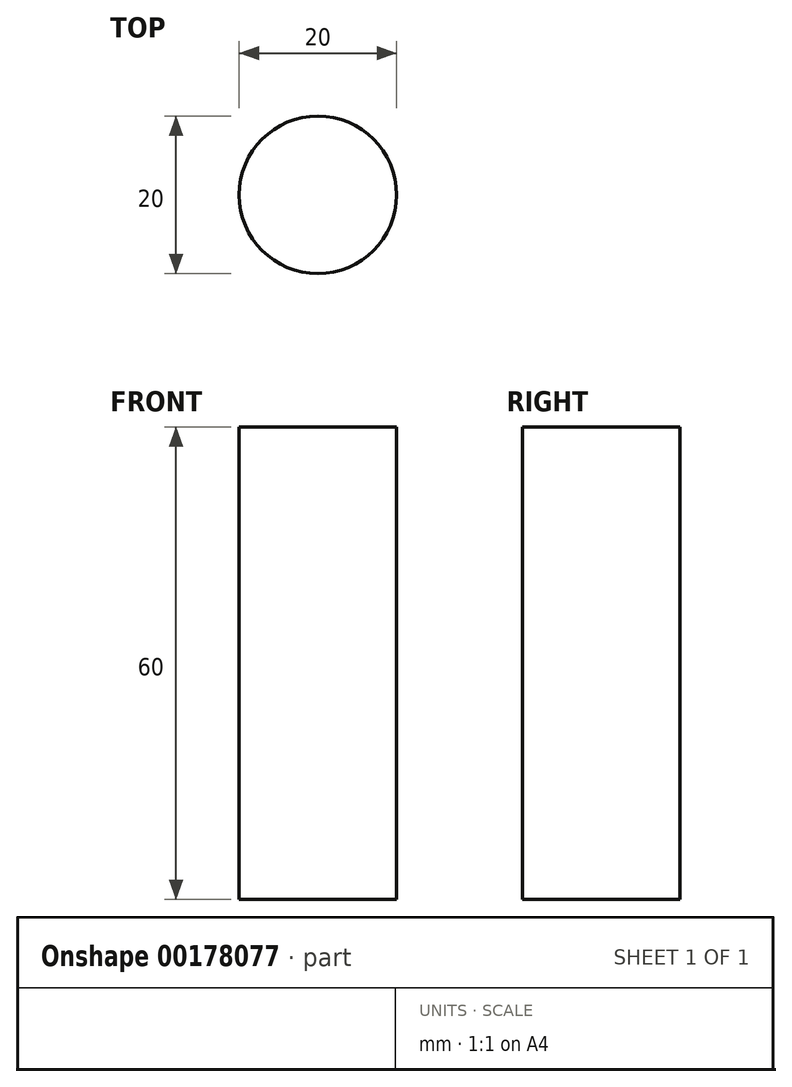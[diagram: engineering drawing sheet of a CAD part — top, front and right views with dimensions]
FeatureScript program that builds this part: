
annotation { "Feature Type Name" : "Feature", "Feature Type Description" : "" }
export const myFeature = defineFeature(function(context is Context, id is Id, definition is map)
    precondition{}
    {
        {
            var Q0;
            Q0=qCreatedBy(makeId("Top.planeOp"),FACE);
            var sketch = newSketch(context, id + "F0", { "sketchPlane" : qUnion([Q0])});
            skCircle(sketch, "E0", {"center": v(0, 0) * mm, "radius": 10 * mm});
            skSolve(sketch);
        }
        {
            var Q0;
            Q0 = qSketchRegion(id + "F0", true);
            extrude(context, id + "F1", {"entities" : qUnion([Q0]), "depth" : 60 * mm});
        }
    });
